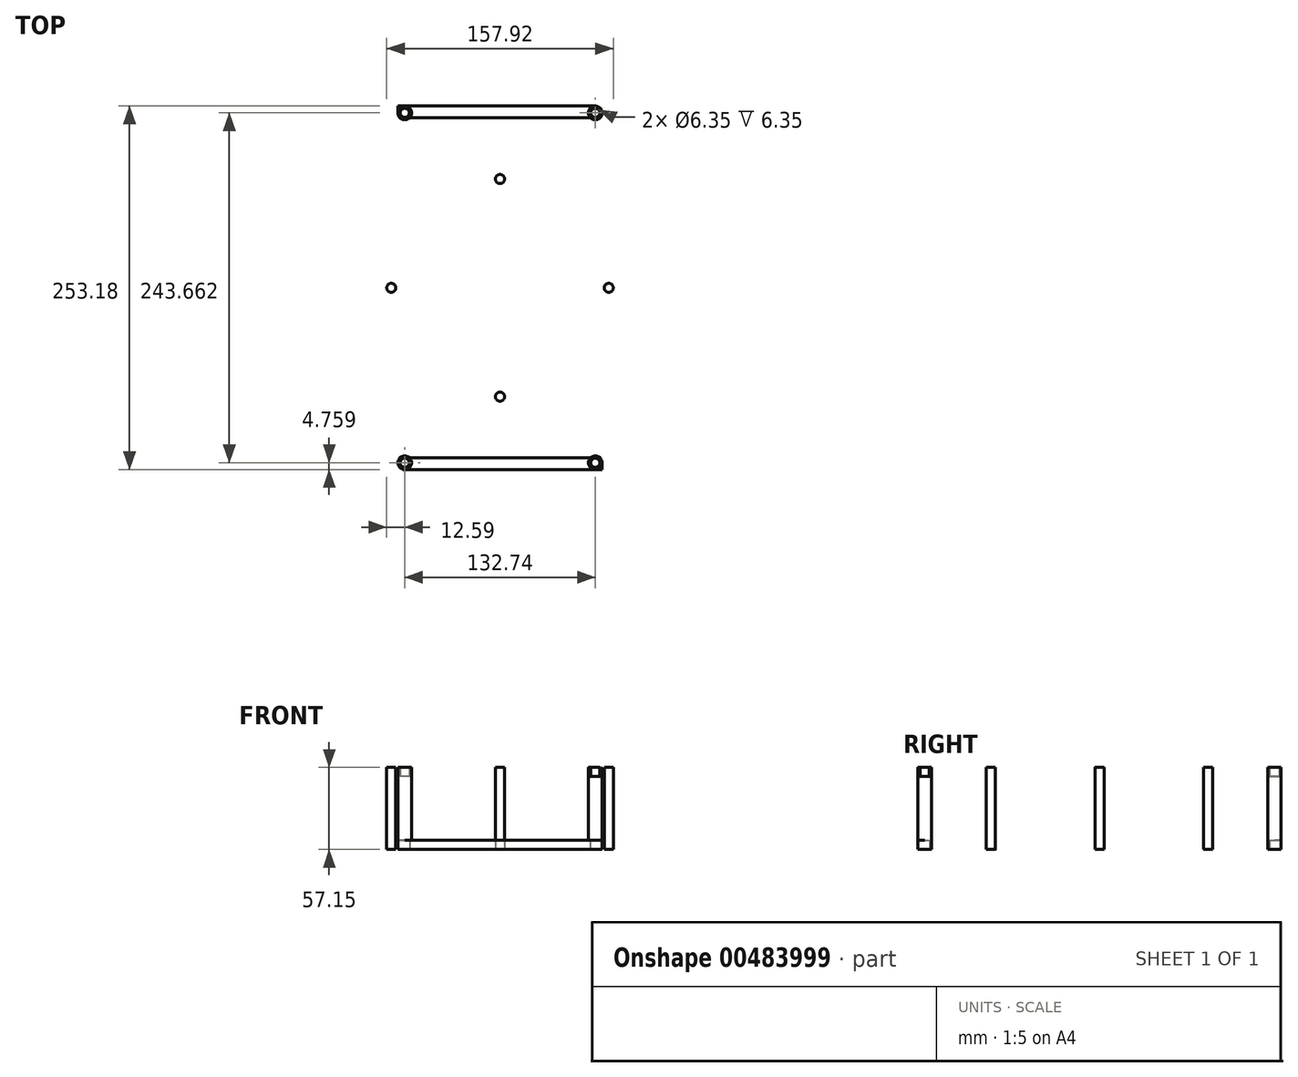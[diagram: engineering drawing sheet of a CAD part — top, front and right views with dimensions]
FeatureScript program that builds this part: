
annotation { "Feature Type Name" : "Feature", "Feature Type Description" : "" }
export const myFeature = defineFeature(function(context is Context, id is Id, definition is map)
    precondition{}
    {
        {
            var Q0;
            Q0=qCreatedBy(makeId("Top.planeOp"),FACE);
            var sketch = newSketch(context, id + "F0", { "sketchPlane" : qUnion([Q0])});
            skLineSegment(sketch, "E0.bottom", {"start": v(-66.37, 121.83) * mm, "end": v(66.37, 121.83) * mm, "construction": true});
            skLineSegment(sketch, "E0.top", {"start": v(-66.37, -121.83) * mm, "end": v(66.37, -121.83) * mm, "construction": true});
            skLineSegment(sketch, "E0.left", {"start": v(-66.37, 121.83) * mm, "end": v(-66.37, -121.83) * mm, "construction": true});
            skLineSegment(sketch, "E0.right", {"start": v(66.37, 121.83) * mm, "end": v(66.37, -121.83) * mm, "construction": true});
            skPoint(sketch, "E0.middle", {"position": v(0, 0) * mm});
            skCircle(sketch, "E1", {"center": v(-66.37, 121.83) * mm, "radius": 3.18 * mm});
            skCircle(sketch, "E2", {"center": v(-66.37, 121.83) * mm, "radius": 4.76 * mm});
            skCircle(sketch, "E3.MirrorC", {"center": v(66.37, 121.83) * mm, "radius": 4.76 * mm});
            skCircle(sketch, "E4.MirrorC", {"center": v(66.37, 121.83) * mm, "radius": 3.18 * mm});
            skCircle(sketch, "E5.MirrorC", {"center": v(-66.37, -121.83) * mm, "radius": 3.18 * mm});
            skCircle(sketch, "E6.MirrorC", {"center": v(-66.37, -121.83) * mm, "radius": 4.76 * mm});
            skCircle(sketch, "E7.MirrorC", {"center": v(66.37, -121.83) * mm, "radius": 3.18 * mm});
            skCircle(sketch, "E8.MirrorC", {"center": v(66.37, -121.83) * mm, "radius": 4.76 * mm});
            skLineSegment(sketch, "E9.bottom", {"start": v(-71.13, 126.6) * mm, "end": v(71.13, 126.6) * mm});
            skLineSegment(sketch, "E9.top", {"start": v(-71.13, -126.6) * mm, "end": v(71.13, -126.6) * mm});
            skLineSegment(sketch, "E9.left", {"start": v(-71.13, 126.6) * mm, "end": v(-71.13, 40.62) * mm});
            skLineSegment(sketch, "E9.right", {"start": v(71.13, 126.6) * mm, "end": v(71.13, 40.62) * mm});
            skLineSegment(sketch, "E10.bottom", {"start": v(-63, 118.46) * mm, "end": v(63, 118.46) * mm});
            skLineSegment(sketch, "E10.top", {"start": v(-63, -118.46) * mm, "end": v(63, -118.46) * mm});
            skLineSegment(sketch, "E10.left", {"start": v(-63, 118.46) * mm, "end": v(-63, 52.35) * mm});
            skLineSegment(sketch, "E10.right", {"start": v(63, 118.46) * mm, "end": v(63, 52.35) * mm});
            skLineSegment(sketch, "E11", {"start": v(64.56, 120.02) * mm, "end": v(50.56, 106.02) * mm, "construction": true});
            skLineSegment(sketch, "E12", {"start": v(-64.05, -119.51) * mm, "end": v(-49.07, -104.53) * mm, "construction": true});
            skCircle(sketch, "E13", {"center": v(0, 0) * mm, "radius": 72.4 * mm});
            skArc(sketch, "E14.0", {"start": v(-71.13, 40.62) * mm, "mid": v(-81.92, 0) * mm, "end": v(-71.13, -40.62) * mm});
            skLineSegment(sketch, "E15.trimOffspring", {"start": v(-63, -52.35) * mm, "end": v(-63, -118.46) * mm});
            skLineSegment(sketch, "E16.trimOffspring", {"start": v(-71.13, -40.62) * mm, "end": v(-71.13, -126.6) * mm});
            skArc(sketch, "E17.trimOffspring", {"start": v(-63, -52.35) * mm, "mid": v(0, -81.92) * mm, "end": v(63, -52.35) * mm});
            skLineSegment(sketch, "E18.trimOffspring", {"start": v(71.13, -40.62) * mm, "end": v(71.13, -126.6) * mm});
            skLineSegment(sketch, "E19.trimOffspring", {"start": v(63, -52.35) * mm, "end": v(63, -118.46) * mm});
            skArc(sketch, "E20.trimOffspring", {"start": v(71.13, -40.62) * mm, "mid": v(81.92, 0) * mm, "end": v(71.13, 40.62) * mm});
            skArc(sketch, "E21.trimOffspring", {"start": v(63, 52.35) * mm, "mid": v(0, 81.92) * mm, "end": v(-63, 52.35) * mm});
            skCircle(sketch, "E22", {"center": v(0, 0) * mm, "radius": 75.78 * mm, "construction": true});
            skCircle(sketch, "E23", {"center": v(0, 75.78) * mm, "radius": 3.18 * mm});
            skCircle(sketch, "E24", {"center": v(-75.78, 0) * mm, "radius": 3.18 * mm});
            skCircle(sketch, "E25", {"center": v(75.78, 0) * mm, "radius": 3.18 * mm});
            skCircle(sketch, "E26", {"center": v(0, -75.78) * mm, "radius": 3.18 * mm});
            skSolve(sketch);
        }
        {
            var Q0;
            {var subQ2=sQuery(id+"F0.wireOp",EDGE,"E10.left");Q0=makeQuery(id+"F0.imprint","IMPRINT",FACE,{"disambiguationData":[TD([[makeQuery(id+"F0.imprint","IMPRINT",EDGE,{"derivedFrom":subQ2}),-1.0]])]});}
            var Q1;
            {var subQ0=sQuery(id+"F0.wireOp",EDGE,"E10.bottom");Q1=makeQuery(id+"F0.imprint","IMPRINT",FACE,{"disambiguationData":[TD([[makeQuery(id+"F0.imprint","IMPRINT",EDGE,{"derivedFrom":subQ0}),1.0]])]});}
            var Q2;
            {var subQ0=sQuery(id+"F0.wireOp",EDGE,"E10.top");Q2=makeQuery(id+"F0.imprint","IMPRINT",FACE,{"disambiguationData":[TD([[makeQuery(id+"F0.imprint","IMPRINT",EDGE,{"derivedFrom":subQ0}),-1.0]])]});}
            var Q3;
            {var subQ0=sQuery(id+"F0.wireOp",EDGE,"E16.trimOffspring");var subQ1=sQuery(id+"F0.wireOp",EDGE,"E6.MirrorC");var subQ2=makeQuery(id+"F0.imprint","INTERSECT",VERTEX,{"derivedFrom":[subQ1,subQ0]});Q3=makeQuery(id+"F0.imprint","IMPRINT",FACE,{"disambiguationData":[TD([[makeQuery(id+"F0.imprint","IMPRINT",EDGE,{"disambiguationData":[TD([[subQ2,1.0]])],"derivedFrom":subQ1}),1.0]])]});}
            var Q4;
            {var subQ0=sQuery(id+"F0.wireOp",EDGE,"E18.trimOffspring");var subQ1=sQuery(id+"F0.wireOp",EDGE,"E8.MirrorC");var subQ2=makeQuery(id+"F0.imprint","INTERSECT",VERTEX,{"derivedFrom":[subQ1,subQ0]});Q4=makeQuery(id+"F0.imprint","IMPRINT",FACE,{"disambiguationData":[TD([[makeQuery(id+"F0.imprint","IMPRINT",EDGE,{"disambiguationData":[TD([[subQ2,1.0]])],"derivedFrom":subQ1}),-1.0]])]});}
            var Q5;
            {var subQ0=sQuery(id+"F0.wireOp",EDGE,"E9.left");var subQ1=sQuery(id+"F0.wireOp",EDGE,"E2");var subQ2=makeQuery(id+"F0.imprint","INTERSECT",VERTEX,{"derivedFrom":[subQ1,subQ0]});Q5=makeQuery(id+"F0.imprint","IMPRINT",FACE,{"disambiguationData":[TD([[makeQuery(id+"F0.imprint","IMPRINT",EDGE,{"disambiguationData":[TD([[subQ2,1.0]])],"derivedFrom":subQ1}),-1.0]])]});}
            var Q6;
            {var subQ0=sQuery(id+"F0.wireOp",EDGE,"E9.right");var subQ1=sQuery(id+"F0.wireOp",EDGE,"E3.MirrorC");var subQ2=makeQuery(id+"F0.imprint","INTERSECT",VERTEX,{"derivedFrom":[subQ1,subQ0]});Q6=makeQuery(id+"F0.imprint","IMPRINT",FACE,{"disambiguationData":[TD([[makeQuery(id+"F0.imprint","IMPRINT",EDGE,{"disambiguationData":[TD([[subQ2,1.0]])],"derivedFrom":subQ1}),1.0]])]});}
            extrude(context, id + "F1", {"entities" : qUnion([Q0, Q1, Q2, Q3, Q4, Q5, Q6]), "depth" : 6.35 * mm});
        }
        {
            var Q0;
            Q0=makeQuery(id+"F0.imprint","IMPRINT",FACE,{"disambiguationData":[TD([[makeQuery(id+"F0.imprint","IMPRINT",EDGE,{"derivedFrom":sQuery(id+"F0.wireOp",EDGE,"E1")}),-1.0]])]});
            var Q1;
            Q1=makeQuery(id+"F0.imprint","IMPRINT",FACE,{"disambiguationData":[TD([[makeQuery(id+"F0.imprint","IMPRINT",EDGE,{"derivedFrom":sQuery(id+"F0.wireOp",EDGE,"E4.MirrorC")}),1.0]])]});
            var Q2;
            Q2=makeQuery(id+"F0.imprint","IMPRINT",FACE,{"disambiguationData":[TD([[makeQuery(id+"F0.imprint","IMPRINT",EDGE,{"derivedFrom":sQuery(id+"F0.wireOp",EDGE,"E5.MirrorC")}),1.0]])]});
            var Q3;
            Q3=makeQuery(id+"F0.imprint","IMPRINT",FACE,{"disambiguationData":[TD([[makeQuery(id+"F0.imprint","IMPRINT",EDGE,{"derivedFrom":sQuery(id+"F0.wireOp",EDGE,"E7.MirrorC")}),-1.0]])]});
            extrude(context, id + "F2", {"entities" : qUnion([Q0, Q1, Q2, Q3]), "operationType" : NewBodyOperationType.ADD, "depth" : 50.8 * mm});
        }
        {
            var Q0;
            Q0=makeQuery(id+"F0.imprint","IMPRINT",FACE,{"disambiguationData":[TD([[makeQuery(id+"F0.imprint","IMPRINT",EDGE,{"derivedFrom":sQuery(id+"F0.wireOp",EDGE,"E7.MirrorC")}),1.0]])]});
            var Q1;
            Q1=makeQuery(id+"F0.imprint","IMPRINT",FACE,{"disambiguationData":[TD([[makeQuery(id+"F0.imprint","IMPRINT",EDGE,{"derivedFrom":sQuery(id+"F0.wireOp",EDGE,"E5.MirrorC")}),-1.0]])]});
            var Q2;
            Q2=makeQuery(id+"F0.imprint","IMPRINT",FACE,{"disambiguationData":[TD([[makeQuery(id+"F0.imprint","IMPRINT",EDGE,{"derivedFrom":sQuery(id+"F0.wireOp",EDGE,"E4.MirrorC")}),-1.0]])]});
            var Q3;
            Q3=makeQuery(id+"F0.imprint","IMPRINT",FACE,{"disambiguationData":[TD([[makeQuery(id+"F0.imprint","IMPRINT",EDGE,{"derivedFrom":sQuery(id+"F0.wireOp",EDGE,"E1")}),1.0]])]});
            extrude(context, id + "F3", {"entities" : qUnion([Q0, Q1, Q2, Q3]), "operationType" : NewBodyOperationType.ADD, "depth" : 57.15 * mm});
        }
        {
            var Q0;
            Q0=makeQuery(id+"F0.imprint","IMPRINT",FACE,{"disambiguationData":[TD([[makeQuery(id+"F0.imprint","IMPRINT",EDGE,{"derivedFrom":sQuery(id+"F0.wireOp",EDGE,"E23")}),1.0]])]});
            var Q1;
            Q1=makeQuery(id+"F0.imprint","IMPRINT",FACE,{"disambiguationData":[TD([[makeQuery(id+"F0.imprint","IMPRINT",EDGE,{"derivedFrom":sQuery(id+"F0.wireOp",EDGE,"E24")}),1.0]])]});
            var Q2;
            Q2=makeQuery(id+"F0.imprint","IMPRINT",FACE,{"disambiguationData":[TD([[makeQuery(id+"F0.imprint","IMPRINT",EDGE,{"derivedFrom":sQuery(id+"F0.wireOp",EDGE,"E25")}),1.0]])]});
            var Q3;
            Q3=makeQuery(id+"F0.imprint","IMPRINT",FACE,{"disambiguationData":[TD([[makeQuery(id+"F0.imprint","IMPRINT",EDGE,{"derivedFrom":sQuery(id+"F0.wireOp",EDGE,"E26")}),1.0]])]});
            extrude(context, id + "F4", {"entities" : qUnion([Q0, Q1, Q2, Q3]), "operationType" : NewBodyOperationType.ADD, "depth" : 57.15 * mm});
        }
    });
